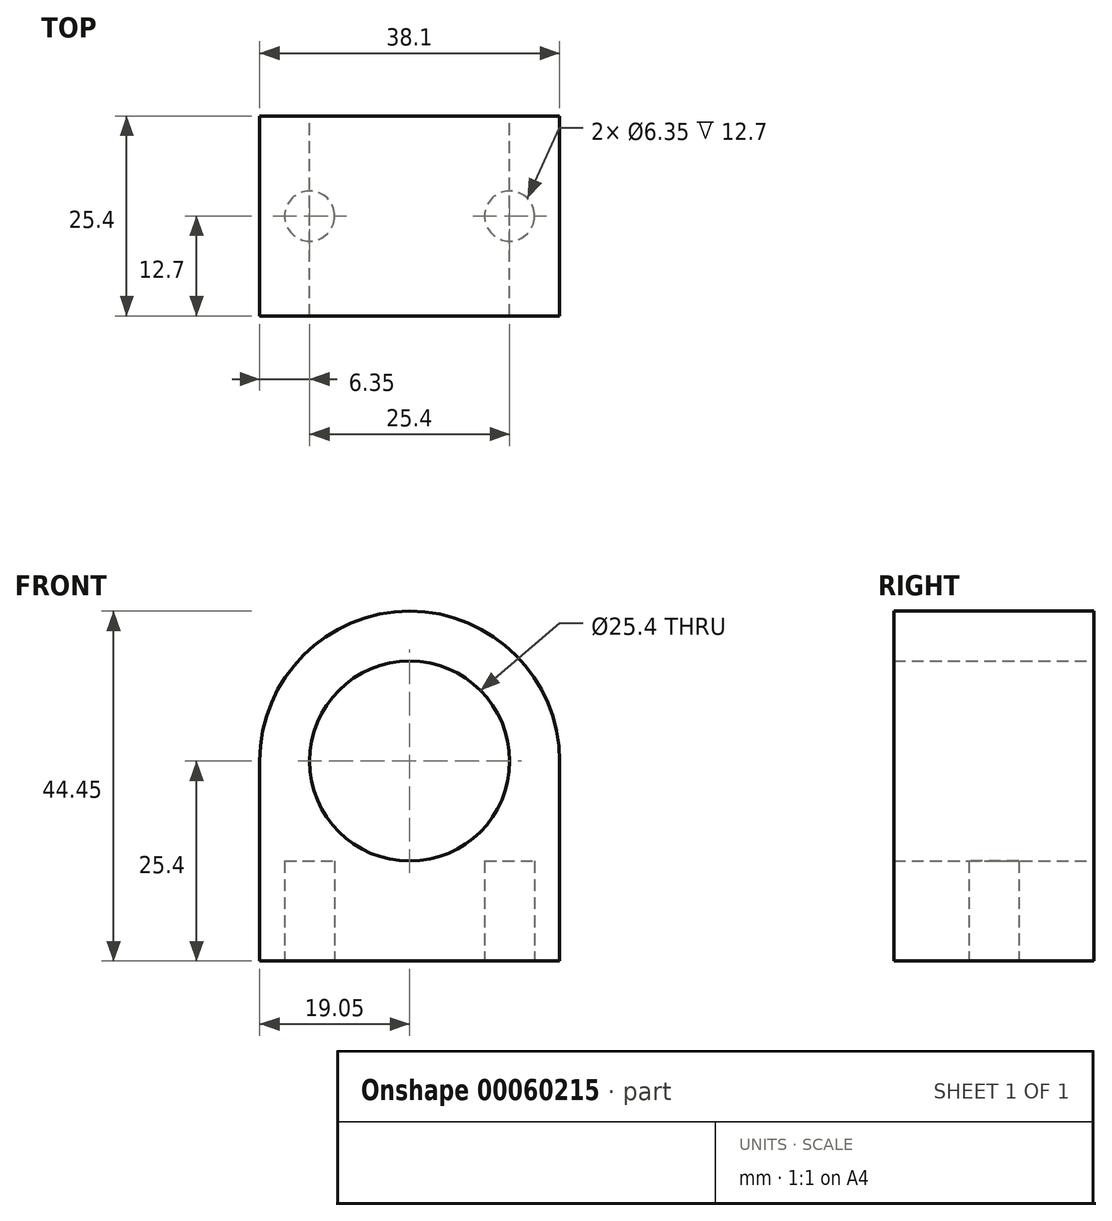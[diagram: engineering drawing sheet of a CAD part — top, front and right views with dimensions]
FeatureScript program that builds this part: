
annotation { "Feature Type Name" : "Feature", "Feature Type Description" : "" }
export const myFeature = defineFeature(function(context is Context, id is Id, definition is map)
    precondition{}
    {
        {
            var Q0;
            Q0=qCreatedBy(makeId("Front.planeOp"),FACE);
            var sketch = newSketch(context, id + "F0", { "sketchPlane" : qUnion([Q0])});
            skCircle(sketch, "E0", {"center": v(0, 0) * mm, "radius": 12.7 * mm});
            skArc(sketch, "E1", {"start": v(19.05, 0) * mm, "mid": v(0, 19.05) * mm, "end": v(-19.05, 0) * mm});
            skLineSegment(sketch, "E2", {"start": v(19.05, 0) * mm, "end": v(19.05, -25.4) * mm});
            skLineSegment(sketch, "E3", {"start": v(-19.05, 0) * mm, "end": v(-19.05, -25.4) * mm});
            skLineSegment(sketch, "E4", {"start": v(-19.05, -25.4) * mm, "end": v(19.05, -25.4) * mm});
            skSolve(sketch);
        }
        {
            var Q0;
            Q0 = qSketchRegion(id + "F0", true);
            extrude(context, id + "F1", {"entities" : qUnion([Q0]), "depth" : 25.4 * mm});
        }
        {
            var Q0;
            Q0=makeQuery(id+"F1.opExtrude","SWEPT_FACE",FACE,{"disambiguationData":[OSD([sQuery(id+"F0.wireOp",EDGE,"E4")])]});
            var sketch = newSketch(context, id + "F2", { "sketchPlane" : qUnion([Q0])});
            skCircle(sketch, "E5", {"center": v(-12.7, 12.7) * mm, "radius": 3.18 * mm});
            skCircle(sketch, "E6", {"center": v(12.7, 12.7) * mm, "radius": 3.18 * mm});
            skSolve(sketch);
        }
        {
            var Q0;
            Q0 = qSketchRegion(id + "F2", true);
            extrude(context, id + "F3", {"entities" : qUnion([Q0]), "operationType" : NewBodyOperationType.REMOVE, "oppositeDirection" : true, "depth" : 12.7 * mm});
        }
    });
